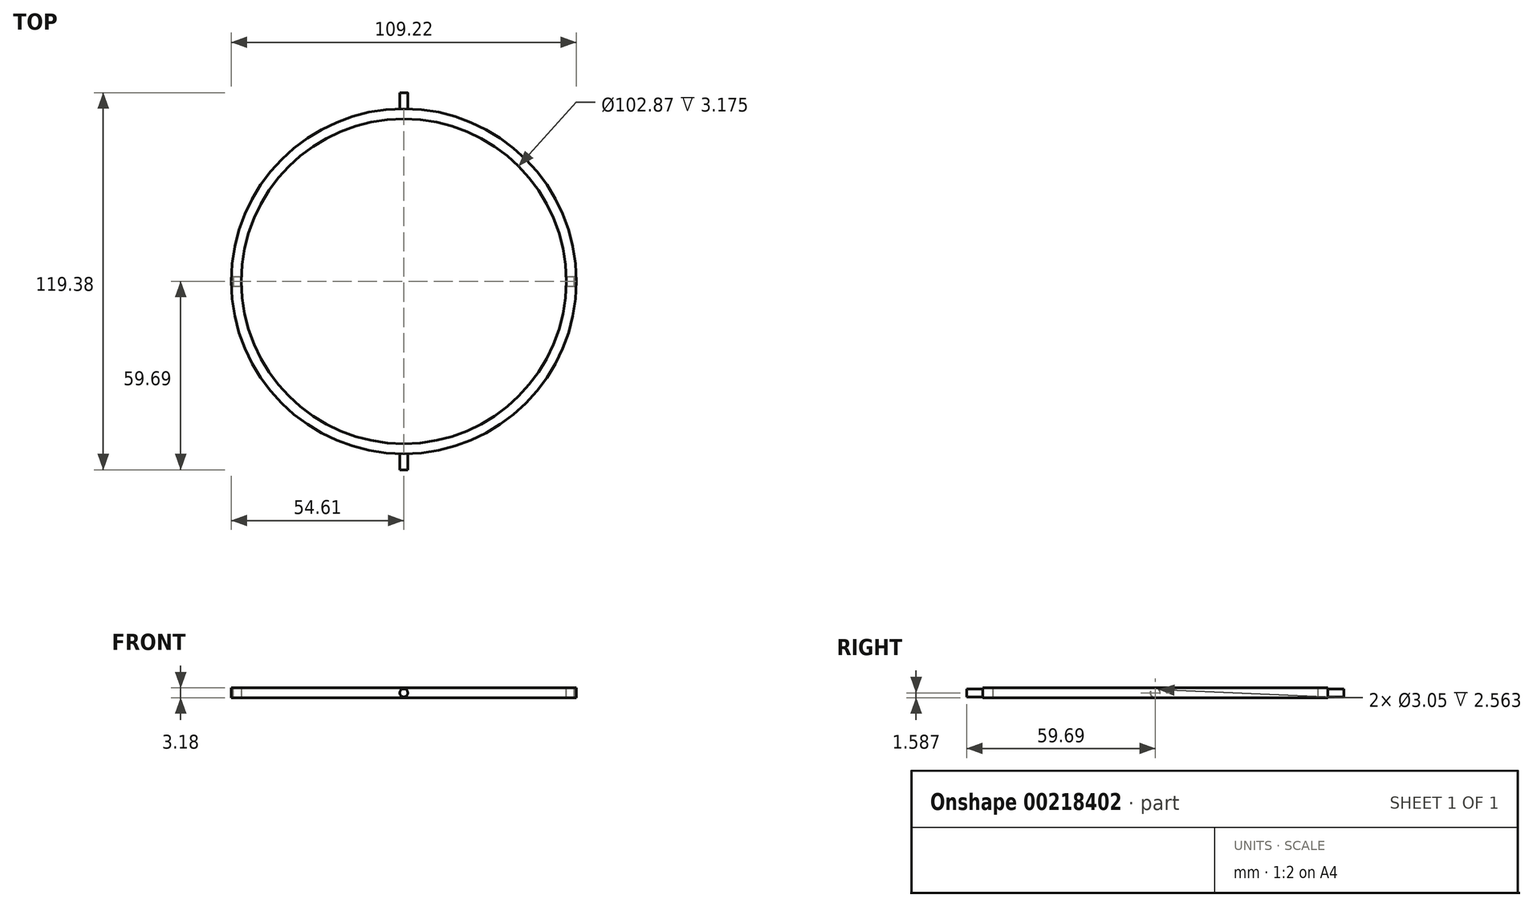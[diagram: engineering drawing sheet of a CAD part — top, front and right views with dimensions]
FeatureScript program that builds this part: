
annotation { "Feature Type Name" : "Feature", "Feature Type Description" : "" }
export const myFeature = defineFeature(function(context is Context, id is Id, definition is map)
    precondition{}
    {
        {
            var Q0;
            Q0=qCreatedBy(makeId("Top.planeOp"),FACE);
            var sketch = newSketch(context, id + "F0", { "sketchPlane" : qUnion([Q0])});
            skCircle(sketch, "E0", {"center": v(0, 0) * mm, "radius": 54.61 * mm});
            skCircle(sketch, "E1", {"center": v(0, 0) * mm, "radius": 51.44 * mm});
            skSolve(sketch);
        }
        {
            var Q0;
            Q0 = qSketchRegion(id + "F0", true);
            extrude(context, id + "F1", {"entities" : qUnion([Q0]), "depth" : 3.17 * mm});
        }
        {
            var Q0;
            Q0=qCreatedBy(makeId("Front.planeOp"),FACE);
            var sketch = newSketch(context, id + "F2", { "sketchPlane" : qUnion([Q0])});
            skLineSegment(sketch, "E2", {"start": v(0, 0) * mm, "end": v(0, 1.59) * mm, "construction": true});
            skCircle(sketch, "E3", {"center": v(0, 1.59) * mm, "radius": 1.27 * mm});
            skSolve(sketch);
        }
        {
            var Q0;
            Q0 = qSketchRegion(id + "F2", true);
            extrude(context, id + "F3", {"entities" : qUnion([Q0]), "operationType" : NewBodyOperationType.ADD, "depth" : 59.69 * mm, "hasSecondDirection" : true, "secondDirectionOppositeDirection" : true, "secondDirectionDepth" : 59.69 * mm});
        }
        {
            var Q0;
            Q0=qCreatedBy(makeId("Top.planeOp"),FACE);
            var sketch = newSketch(context, id + "F4", { "sketchPlane" : qUnion([Q0])});
            skCircle(sketch, "E4", {"center": v(0, 0) * mm, "radius": 51.44 * mm});
            skSolve(sketch);
        }
        {
            var Q0;
            Q0 = qSketchRegion(id + "F4", true);
            extrude(context, id + "F5", {"entities" : qUnion([Q0]), "operationType" : NewBodyOperationType.REMOVE, "depth" : 25.4 * mm});
        }
        {
            var Q0;
            Q0=qCreatedBy(makeId("Right.planeOp"),FACE);
            var sketch = newSketch(context, id + "F6", { "sketchPlane" : qUnion([Q0])});
            skLineSegment(sketch, "E5", {"start": v(0, 0) * mm, "end": v(0, 1.59) * mm, "construction": true});
            skCircle(sketch, "E6", {"center": v(0, 1.59) * mm, "radius": 1.52 * mm});
            skSolve(sketch);
        }
        {
            var Q0;
            Q0 = qSketchRegion(id + "F6", true);
            extrude(context, id + "F7", {"entities" : qUnion([Q0]), "operationType" : NewBodyOperationType.REMOVE, "oppositeDirection" : true, "depth" : 53.97 * mm, "hasSecondDirection" : true, "secondDirectionOppositeDirection" : false, "secondDirectionDepth" : 53.97 * mm});
        }
    });
